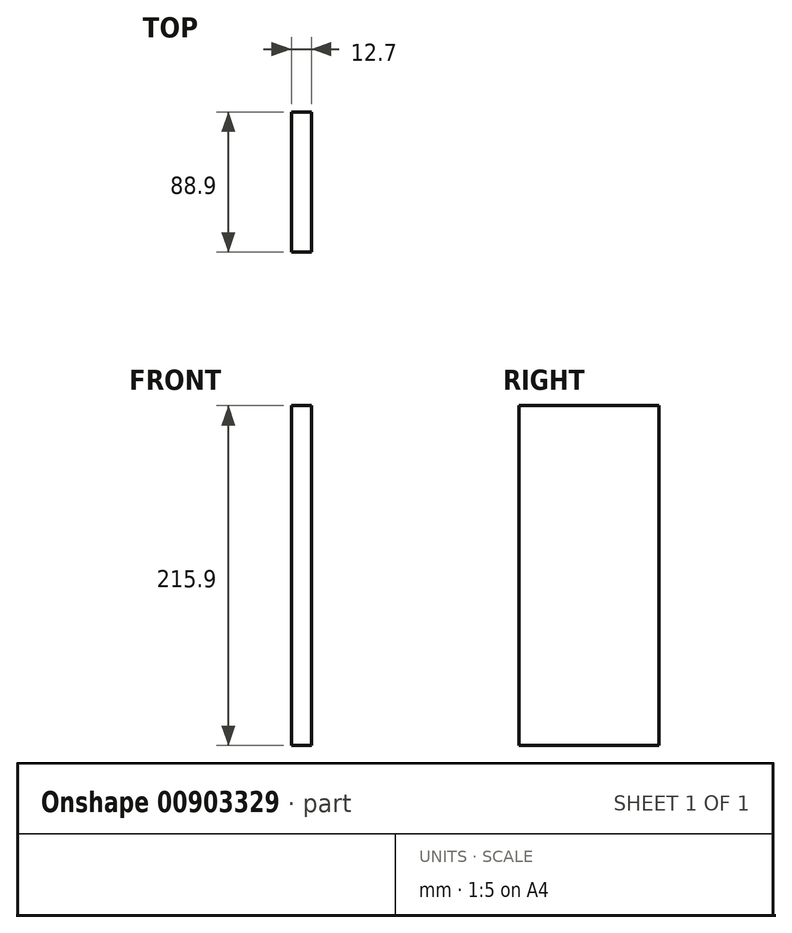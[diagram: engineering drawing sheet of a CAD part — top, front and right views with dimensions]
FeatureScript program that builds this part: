
annotation { "Feature Type Name" : "Feature", "Feature Type Description" : "" }
export const myFeature = defineFeature(function(context is Context, id is Id, definition is map)
    precondition{}
    {
        {
            var Q0;
            Q0=qCreatedBy(makeId("Right.planeOp"),FACE);
            var sketch = newSketch(context, id + "F0", { "sketchPlane" : qUnion([Q0])});
            skLineSegment(sketch, "E0.bottom", {"start": v(-61.42, 141.14) * mm, "end": v(27.48, 141.14) * mm});
            skLineSegment(sketch, "E0.top", {"start": v(-61.42, -74.76) * mm, "end": v(27.48, -74.76) * mm});
            skLineSegment(sketch, "E0.left", {"start": v(-61.42, 141.14) * mm, "end": v(-61.42, -74.76) * mm});
            skLineSegment(sketch, "E0.right", {"start": v(27.48, 141.14) * mm, "end": v(27.48, -74.76) * mm});
            skSolve(sketch);
        }
        {
            var Q0;
            Q0=makeQuery(id+"F0.imprint","IMPRINT",FACE,{"disambiguationData":[TD([[makeQuery(id+"F0.imprint","IMPRINT",EDGE,{"derivedFrom":sQuery(id+"F0.wireOp",EDGE,"E0.bottom")}),-1.0]])]});
            extrude(context, id + "F1", {"entities" : qUnion([Q0]), "depth" : 12.7 * mm, "offsetDistance" : 25.4 * mm});
        }
    });
